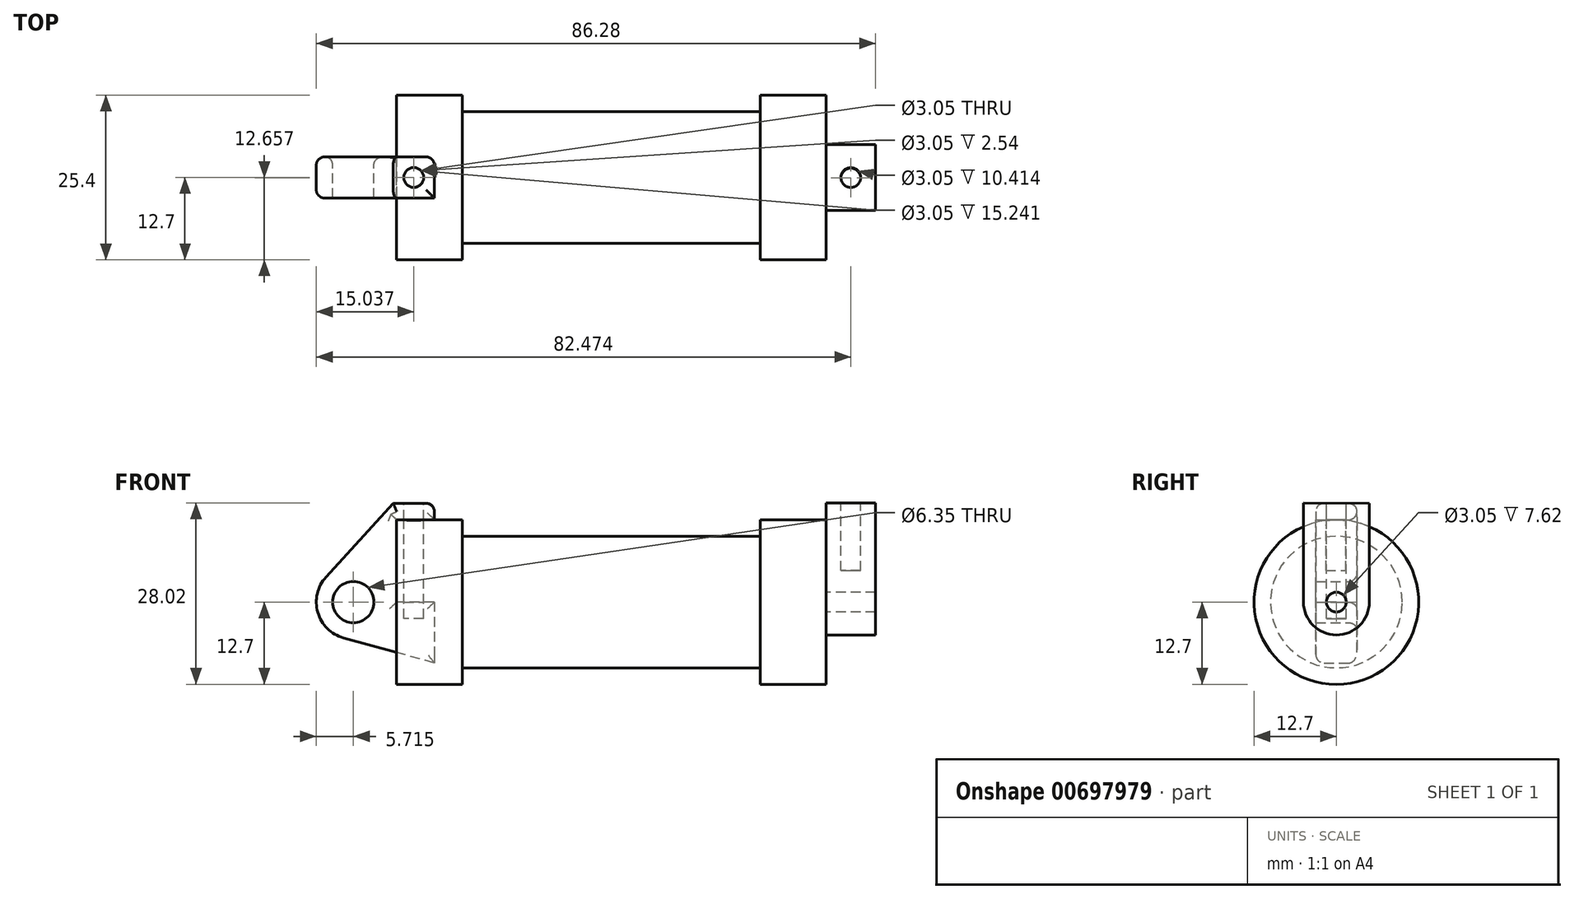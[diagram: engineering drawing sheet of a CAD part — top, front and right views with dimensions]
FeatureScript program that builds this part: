
annotation { "Feature Type Name" : "Feature", "Feature Type Description" : "" }
export const myFeature = defineFeature(function(context is Context, id is Id, definition is map)
    precondition{}
    {
        {
            var Q0;
            Q0=qCreatedBy(makeId("Front.planeOp"),FACE);
            var sketch = newSketch(context, id + "F0", { "sketchPlane" : qUnion([Q0])});
            skLineSegment(sketch, "E0", {"start": v(0, 0) * mm, "end": v(0, 12.7) * mm});
            skLineSegment(sketch, "E1", {"start": v(0, 12.7) * mm, "end": v(10.16, 12.7) * mm});
            skLineSegment(sketch, "E2", {"start": v(10.16, 12.7) * mm, "end": v(10.16, 10.16) * mm});
            skLineSegment(sketch, "E3", {"start": v(10.16, 10.16) * mm, "end": v(56.13, 10.16) * mm});
            skLineSegment(sketch, "E4", {"start": v(56.13, 10.16) * mm, "end": v(56.13, 12.7) * mm});
            skLineSegment(sketch, "E5", {"start": v(56.13, 12.7) * mm, "end": v(66.3, 12.7) * mm});
            skLineSegment(sketch, "E6", {"start": v(66.3, 12.7) * mm, "end": v(66.3, 0) * mm});
            skLineSegment(sketch, "E7", {"start": v(66.3, 0) * mm, "end": v(0, 0) * mm});
            skLineSegment(sketch, "E8", {"start": v(5.84, 15.24) * mm, "end": v(-0.5, 15.24) * mm});
            skLineSegment(sketch, "E9", {"start": v(-0.5, 15.24) * mm, "end": v(-10.88, 3.85) * mm});
            skLineSegment(sketch, "E10", {"start": v(0, 0) * mm, "end": v(-6.65, 0) * mm});
            skCircle(sketch, "E11", {"center": v(-6.65, 0) * mm, "radius": 5.72 * mm});
            skCircle(sketch, "E12", {"center": v(-6.65, 0) * mm, "radius": 3.18 * mm});
            skLineSegment(sketch, "E13", {"start": v(5.84, 15.24) * mm, "end": v(5.84, -9.4) * mm});
            skLineSegment(sketch, "E14", {"start": v(5.84, -9.4) * mm, "end": v(-8.18, -5.5) * mm});
            skSolve(sketch);
        }
        {
            var Q0;
            {var subQ0=sQuery(id+"F0.wireOp",EDGE,"E2");Q0=makeQuery(id+"F0.imprint","IMPRINT",FACE,{"disambiguationData":[TD([[makeQuery(id+"F0.imprint","IMPRINT",EDGE,{"derivedFrom":subQ0}),-1.0]])]});}
            var Q1;
            {var subQ0=sQuery(id+"F0.wireOp",EDGE,"E0");Q1=makeQuery(id+"F0.imprint","IMPRINT",FACE,{"disambiguationData":[TD([[makeQuery(id+"F0.imprint","IMPRINT",EDGE,{"derivedFrom":subQ0}),-1.0]])]});}
            var Q2;
            Q2=sQuery(id+"F0.wireOp",EDGE,"E7");
            revolve(context, id + "F1", {"entities" : qUnion([Q0, Q1]), "axis" : qUnion([Q2]), "revolveType" : RevolveType.FULL});
        }
        {
            var Q0;
            {var subQ0=sQuery(id+"F0.wireOp",EDGE,"E14");Q0=makeQuery(id+"F0.imprint","IMPRINT",FACE,{"disambiguationData":[TD([[makeQuery(id+"F0.imprint","IMPRINT",EDGE,{"derivedFrom":subQ0}),-1.0]])]});}
            var Q1;
            {var subQ5=sQuery(id+"F0.wireOp",EDGE,"E12");Q1=makeQuery(id+"F0.imprint","IMPRINT",FACE,{"disambiguationData":[TD([[makeQuery(id+"F0.imprint","IMPRINT",EDGE,{"derivedFrom":subQ5}),-1.0]])]});}
            var Q2;
            {var subQ1=sQuery(id+"F0.wireOp",EDGE,"E0");Q2=makeQuery(id+"F0.imprint","IMPRINT",FACE,{"disambiguationData":[TD([[makeQuery(id+"F0.imprint","IMPRINT",EDGE,{"derivedFrom":subQ1}),1.0]])]});}
            extrude(context, id + "F2", {"entities" : qUnion([Q0, Q1, Q2]), "depth" : 6.35 * mm, "offsetDistance" : 25.4 * mm, "symmetric" : true});
        }
        {
            var Q0;
            Q0=makeQuery(id+"F1.opRevolve","SWEPT_FACE",FACE,{"disambiguationData":[OSD([sQuery(id+"F0.wireOp",EDGE,"E6")])]});
            var sketch = newSketch(context, id + "F3", { "sketchPlane" : qUnion([Q0])});
            skCircle(sketch, "E15", {"center": v(0, 0) * mm, "radius": 1.52 * mm});
            skCircle(sketch, "E16", {"center": v(0, 0) * mm, "radius": 5.08 * mm});
            skLineSegment(sketch, "E17", {"start": v(5.08, -0.02) * mm, "end": v(5.08, 15.24) * mm});
            skLineSegment(sketch, "E18", {"start": v(-5.08, 0) * mm, "end": v(-5.08, 15.32) * mm});
            skLineSegment(sketch, "E19", {"start": v(-5.08, 15.32) * mm, "end": v(5.08, 15.24) * mm});
            skSolve(sketch);
        }
        {
            var Q0;
            {var subQ0=sQuery(id+"F3.wireOp",EDGE,"E19");Q0=makeQuery(id+"F3.imprint","IMPRINT",FACE,{"disambiguationData":[TD([[makeQuery(id+"F3.imprint","IMPRINT",EDGE,{"derivedFrom":subQ0}),-1.0]])]});}
            var Q1;
            {var subQ0=sQuery(id+"F3.wireOp",EDGE,"E17");var subQ1=sQuery(id+"F3.wireOp",EDGE,"E16");var subQ2=makeQuery(id+"F3.imprint","INTERSECT",VERTEX,{"derivedFrom":[subQ1,subQ0]});Q1=makeQuery(id+"F3.imprint","IMPRINT",FACE,{"disambiguationData":[TD([[makeQuery(id+"F3.imprint","IMPRINT",EDGE,{"disambiguationData":[TD([[subQ2,-1.0]])],"derivedFrom":subQ1}),-1.0]])]});}
            var Q2;
            Q2=makeQuery(id+"F3.imprint","IMPRINT",FACE,{"disambiguationData":[TD([[makeQuery(id+"F3.imprint","IMPRINT",EDGE,{"derivedFrom":sQuery(id+"F3.wireOp",EDGE,"E15")}),-1.0]])]});
            extrude(context, id + "F4", {"entities" : qUnion([Q0, Q1, Q2]), "operationType" : NewBodyOperationType.ADD, "depth" : 7.62 * mm, "offsetDistance" : 25.4 * mm});
        }
        {
            var Q0;
            Q0=makeQuery(id+"F4.opExtrude","SWEPT_FACE",FACE,{"disambiguationData":[OSD([sQuery(id+"F3.wireOp",EDGE,"E19")])]});
            var sketch = newSketch(context, id + "F5", { "sketchPlane" : qUnion([Q0])});
            skCircle(sketch, "E20", {"center": v(70.1, -0.13) * mm, "radius": 1.52 * mm});
            skSolve(sketch);
        }
        {
            var Q0;
            Q0=makeQuery(id+"F5.imprint","IMPRINT",FACE,{"disambiguationData":[TD([[makeQuery(id+"F5.imprint","IMPRINT",EDGE,{"derivedFrom":sQuery(id+"F5.wireOp",EDGE,"E20")}),1.0]])]});
            var Q1;
            Q1 = qSketchRegion(id + "F5", true);
            extrude(context, id + "F6", {"entities" : qUnion([Q0, Q1]), "operationType" : NewBodyOperationType.REMOVE, "oppositeDirection" : true, "depth" : 10.4 * mm, "offsetDistance" : 25.4 * mm});
        }
        {
            var Q0;
            Q0=makeQuery(id+"F2.opExtrude","SWEPT_FACE",FACE,{"disambiguationData":[OSD([sQuery(id+"F0.wireOp",EDGE,"E8")])]});
            var sketch = newSketch(context, id + "F7", { "sketchPlane" : qUnion([Q0])});
            skCircle(sketch, "E21", {"center": v(2.67, 0) * mm, "radius": 1.52 * mm});
            skSolve(sketch);
        }
        {
            var Q0;
            Q0=makeQuery(id+"F7.imprint","IMPRINT",FACE,{"disambiguationData":[TD([[makeQuery(id+"F7.imprint","IMPRINT",EDGE,{"derivedFrom":sQuery(id+"F7.wireOp",EDGE,"E21")}),1.0]])]});
            extrude(context, id + "F8", {"entities" : qUnion([Q0]), "operationType" : NewBodyOperationType.REMOVE, "oppositeDirection" : true, "depth" : 17.78 * mm, "offsetDistance" : 25.4 * mm});
        }
        {
            var Q0;
            {var subQ0=sQuery(id+"F0.wireOp",EDGE,"E5");var subQ1=sQuery(id+"F0.wireOp",EDGE,"E6");Q0=makeQuery(id+"F4.boolean.opBoolean","SPLIT",EDGE,{"disambiguationData":[topologyDisambiguationEdgeConnected([makeQuery(id+"F1.opRevolve","SWEPT_FACE",FACE,{"disambiguationData":[OSD([subQ1])]})])],"derivedFrom":makeQuery(id+"F1.opRevolve","SWEPT_EDGE",EDGE,{"disambiguationData":[OSD([subQ0,subQ1])]})});}
            var Q1;
            Q1=makeQuery(id+"F4.opExtrude","SWEPT_EDGE",EDGE,{"disambiguationData":[OSD([sQuery(id+"F3.wireOp",EDGE,"E18"),sQuery(id+"F3.wireOp",EDGE,"E19")])]});
            var Q2;
            Q2=makeQuery(id+"F4.opExtrude","CAP_EDGE",EDGE,{"disambiguationData":[OSD([sQuery(id+"F3.wireOp",EDGE,"E18")])],"isStart":false});
            var Q3;
            Q3=makeQuery(id+"F4.opExtrude","CAP_EDGE",EDGE,{"disambiguationData":[OSD([sQuery(id+"F3.wireOp",EDGE,"E19")])],"isStart":false});
            var Q4;
            Q4=makeQuery(id+"F4.opExtrude","SWEPT_FACE",FACE,{"disambiguationData":[OSD([sQuery(id+"F3.wireOp",EDGE,"E19")])]});
            var Q5;
            Q5=makeQuery(id+"F1.opRevolve","SWEPT_EDGE",EDGE,{"disambiguationData":[OSD([sQuery(id+"F0.wireOp",EDGE,"E4"),sQuery(id+"F0.wireOp",EDGE,"E5")])]});
            var Q6;
            {var subQ0=sQuery(id+"F0.wireOp",EDGE,"E13");Q6=makeQuery(id+"F2.opExtrude","CAP_EDGE",EDGE,{"disambiguationData":[OSD([subQ0]),TDD([makeQuery(id+"F0.imprint","IMPRINT",EDGE,{"disambiguationData":[TD([[makeQuery(id+"F0.imprint","INTERSECT",VERTEX,{"derivedFrom":[sQuery(id+"F0.wireOp",EDGE,"E8"),subQ0]}),-1.0]])],"derivedFrom":subQ0})])],"isStart":true});}
            var Q7;
            Q7=makeQuery(id+"F1.opRevolve","SWEPT_EDGE",EDGE,{"disambiguationData":[OSD([sQuery(id+"F0.wireOp",EDGE,"E1"),sQuery(id+"F0.wireOp",EDGE,"E2")])]});
            var Q8;
            Q8=makeQuery(id+"F1.opRevolve","SWEPT_EDGE",EDGE,{"disambiguationData":[OSD([sQuery(id+"F0.wireOp",EDGE,"E0"),sQuery(id+"F0.wireOp",EDGE,"E1")])]});
            var Q9;
            Q9=makeQuery(id+"F2.opExtrude","CAP_FACE",FACE,{"disambiguationData":[OSD([sQuery(id+"F0.wireOp",EDGE,"E0"),sQuery(id+"F0.wireOp",EDGE,"E1"),sQuery(id+"F0.wireOp",EDGE,"E7"),sQuery(id+"F0.wireOp",EDGE,"E8"),sQuery(id+"F0.wireOp",EDGE,"E9"),sQuery(id+"F0.wireOp",EDGE,"E11"),sQuery(id+"F0.wireOp",EDGE,"E12"),sQuery(id+"F0.wireOp",EDGE,"E13"),sQuery(id+"F0.wireOp",EDGE,"E14")])],"isStart":true});
            var Q10;
            Q10=makeQuery(id+"F2.opExtrude","CAP_EDGE",EDGE,{"disambiguationData":[OSD([sQuery(id+"F0.wireOp",EDGE,"E9")])],"isStart":false});
            var Q11;
            Q11=makeQuery(id+"F2.opExtrude","CAP_EDGE",EDGE,{"disambiguationData":[OSD([sQuery(id+"F0.wireOp",EDGE,"E8")])],"isStart":false});
            var Q12;
            Q12=makeQuery(id+"F2.opExtrude","SWEPT_EDGE",EDGE,{"disambiguationData":[OSD([sQuery(id+"F0.wireOp",EDGE,"E8"),sQuery(id+"F0.wireOp",EDGE,"E13")])]});
            fillet(context, id + "F9", {"entities" : qUnion([Q0, Q1, Q2, Q3, Q4, Q5, Q6, Q7, Q8, Q9, Q10, Q11, Q12]), "radius" : 1.27 * mm, "tangentPropagation" : true, "allowEdgeOverflow" : false});
        }
    });
